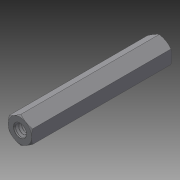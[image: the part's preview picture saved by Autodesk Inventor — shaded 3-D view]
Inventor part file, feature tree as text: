
AUTODESK INVENTOR PART (.ipt)
format: ipt  version: 2015 (Build 190159000, 159)  size: 792,576 bytes
history: native  units: in
note: dims shown in document units (in); Inventor stores cm internally (conversion verified against a paired STEP export)
features: hole x10, sketch x6, other x1, imported_body x1
ambient origin geometry x8: Origin, YZ Plane, XZ Plane, XY Plane, X Axis, Y Axis, Z Axis, Center Point
bodies: Solid1 (feature_tree)
feature tree (18):
  other  "91780A337.sat1"
  hole  "Hole1"  [1 undecoded]
  hole  "Hole2"  [1 undecoded]
  hole  "Hole4"  [1 undecoded]
  hole  "Hole6"  [1 undecoded]
  hole  "Hole8"  [1 undecoded]
  hole  "Hole10"  [1 undecoded]
  imported_body  "Base1"
  sketch  "Sketch1"  dims[d0=0.142in d1=0.75in d2=0.375in d3=0.25in d4=0.5635in d5=0.001in d6=0.8108in]
  sketch  "Sketch2"  dims[d7=0.142in d8=0.75in d9=0.375in d10=0.25in d11=0.5635in d12=0.001in d13=0.8108in]
  sketch  "Sketch3"  dims[d14=0.104in d15=0.319in d16=0.375in d17=0.25in d18=0.5635in d19=0.388in d20=120.0deg]
  hole  "Hole3"  [1 undecoded]
  sketch  "Sketch4"  dims[d21=0.104in d22=0.319in d23=0.375in d24=0.25in d25=0.5635in d26=0.388in d27=120.0deg]
  hole  "Hole5"  [1 undecoded]
  sketch  "Sketch5"  dims[d28=0.104in d29=0.319in d30=0.375in d31=0.25in d32=0.5635in d33=0.388in d34=120.0deg]
  hole  "Hole7"  [1 undecoded]
  sketch  "Sketch6"  dims[d35=0.104in d36=0.319in d37=0.375in d38=0.25in d39=0.5635in d40=0.388in d41=120.0deg]
  hole  "Hole9"  [1 undecoded]
note: 10 required parameter values undecoded (feature->parameter linkage not recoverable at this tier; creation-order binding heuristic only, values carry confidence <= 0.55)
